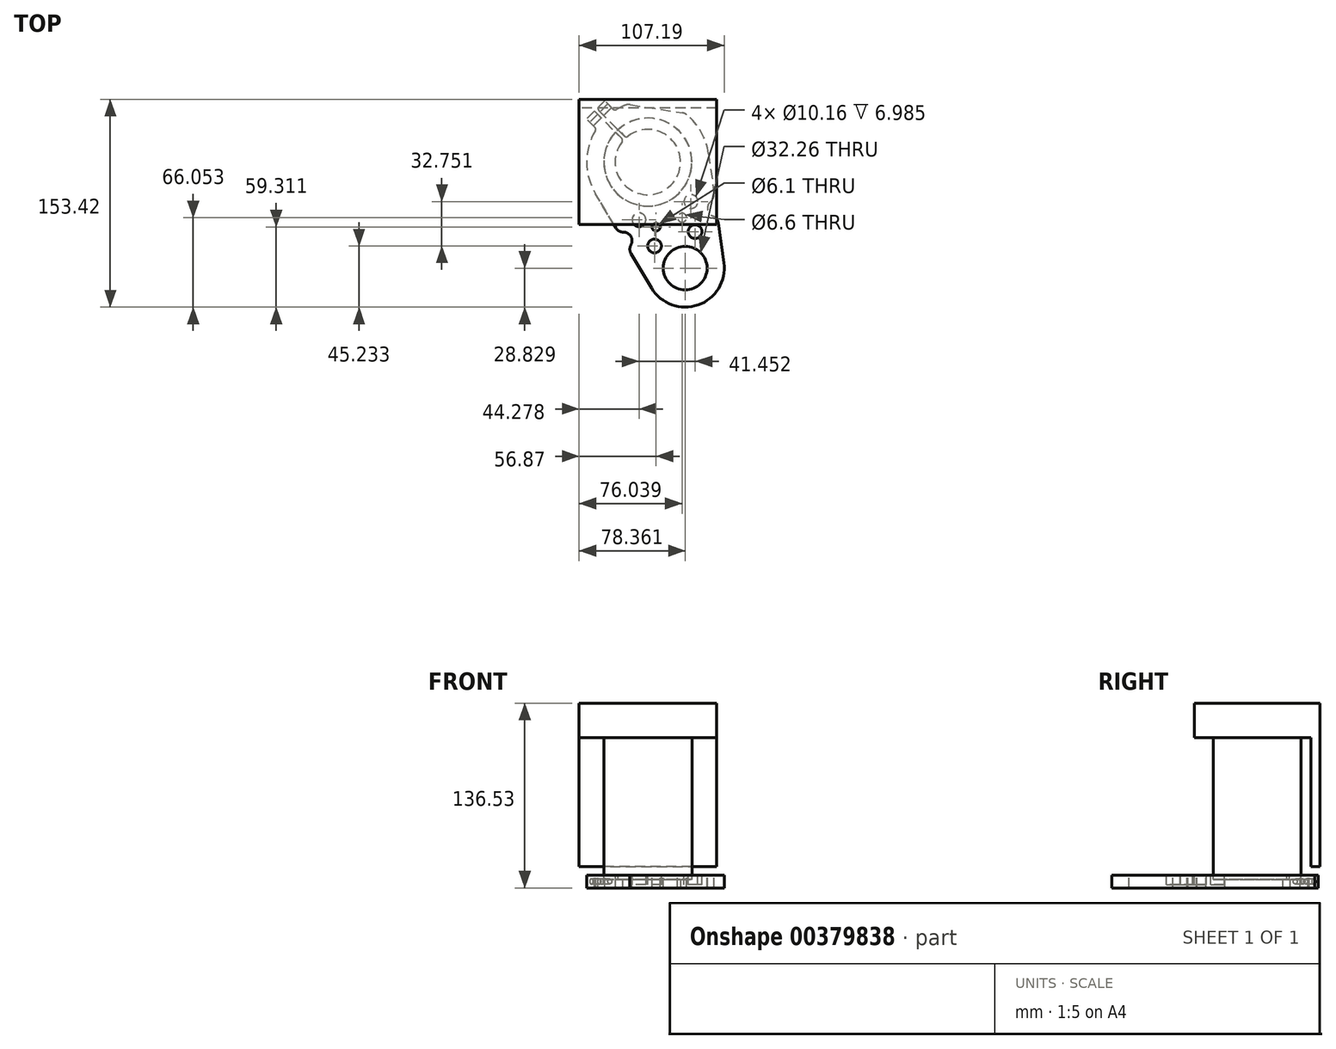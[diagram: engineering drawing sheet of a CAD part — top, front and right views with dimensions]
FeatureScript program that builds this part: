
annotation { "Feature Type Name" : "Feature", "Feature Type Description" : "" }
export const myFeature = defineFeature(function(context is Context, id is Id, definition is map)
    precondition{}
    {
        {
            var Q0;
            Q0=qCreatedBy(makeId("Top.planeOp"),FACE);
            var sketch = newSketch(context, id + "F0", { "sketchPlane" : qUnion([Q0])});
            skLineSegment(sketch, "E0.bottom", {"start": v(0, 0) * mm, "end": v(101.6, 0) * mm});
            skLineSegment(sketch, "E0.top", {"start": v(0, 152.4) * mm, "end": v(101.6, 152.4) * mm});
            skLineSegment(sketch, "E0.left", {"start": v(0, 0) * mm, "end": v(0, 152.4) * mm});
            skLineSegment(sketch, "E0.right", {"start": v(101.6, 0) * mm, "end": v(101.6, 152.4) * mm});
            skSolve(sketch);
        }
        {
            var Q0;
            Q0 = qSketchRegion(id + "F0", true);
            extrude(context, id + "F1", {"entities" : qUnion([Q0]), "depth" : 9.52 * mm});
        }
        {
            var Q0;
            Q0=makeQuery(id+"F1.opExtrude","CAP_FACE",FACE,{"disambiguationData":[OSD([sQuery(id+"F0.wireOp",EDGE,"E0.bottom"),sQuery(id+"F0.wireOp",EDGE,"E0.top"),sQuery(id+"F0.wireOp",EDGE,"E0.left"),sQuery(id+"F0.wireOp",EDGE,"E0.right")])],"isStart":false});
            var sketch = newSketch(context, id + "F2", { "sketchPlane" : qUnion([Q0])});
            skCircle(sketch, "E1", {"center": v(45.21, 107.19) * mm, "radius": 32.51 * mm});
            skCircle(sketch, "E2", {"center": v(72.77, 28.83) * mm, "radius": 16.13 * mm});
            skLineSegment(sketch, "E3", {"start": v(29.31, 152.4) * mm, "end": v(82.91, 0) * mm, "construction": true});
            skLineSegment(sketch, "E4", {"start": v(0, 152.4) * mm, "end": v(22.22, 130.18) * mm, "construction": true});
            skSolve(sketch);
        }
        {
            var Q0;
            Q0 = qSketchRegion(id + "F2", true);
            extrude(context, id + "F3", {"entities" : qUnion([Q0]), "operationType" : NewBodyOperationType.REMOVE, "oppositeDirection" : true, "depth" : 25.4 * mm});
        }
        {
            var Q0;
            Q0=makeQuery(id+"F1.opExtrude","CAP_FACE",FACE,{"disambiguationData":[OSD([sQuery(id+"F0.wireOp",EDGE,"E0.bottom"),sQuery(id+"F0.wireOp",EDGE,"E0.top"),sQuery(id+"F0.wireOp",EDGE,"E0.left"),sQuery(id+"F0.wireOp",EDGE,"E0.right")])],"isStart":false});
            var sketch = newSketch(context, id + "F4", { "sketchPlane" : qUnion([Q0])});
            skArc(sketch, "E5", {"start": v(89.98, 113.48) * mm, "mid": v(84.17, 130.12) * mm, "end": v(72.44, 143.28) * mm});
            skArc(sketch, "E6", {"start": v(48, 14.09) * mm, "mid": v(82.34, 1.63) * mm, "end": v(101.32, 32.84) * mm});
            skLineSegment(sketch, "E7", {"start": v(48, 14.09) * mm, "end": v(30.42, 43.62) * mm});
            skLineSegment(sketch, "E8", {"start": v(89.98, 113.48) * mm, "end": v(94.77, 79.45) * mm});
            skLineSegment(sketch, "E9", {"start": v(0, 152.4) * mm, "end": v(22.22, 130.18) * mm, "construction": true});
            skLineSegment(sketch, "E10", {"start": v(7.22, 131.7) * mm, "end": v(0, 138.93) * mm});
            skLineSegment(sketch, "E11", {"start": v(20.7, 145.18) * mm, "end": v(13.47, 152.4) * mm});
            skLineSegment(sketch, "E12", {"start": v(13.47, 152.4) * mm, "end": v(0, 138.93) * mm});
            skArc(sketch, "E13.trimOffspring", {"start": v(7.22, 131.7) * mm, "mid": v(0, 108.01) * mm, "end": v(6.36, 84.07) * mm});
            skArc(sketch, "E14", {"start": v(94.77, 79.45) * mm, "mid": v(89.36, 72.28) * mm, "end": v(96.54, 66.87) * mm});
            skArc(sketch, "E15", {"start": v(23.93, 54.54) * mm, "mid": v(32.63, 52.33) * mm, "end": v(30.42, 43.62) * mm});
            skLineSegment(sketch, "E16.trimOffspring", {"start": v(96.54, 66.87) * mm, "end": v(101.32, 32.84) * mm});
            skLineSegment(sketch, "E17.trimOffspring", {"start": v(23.93, 54.54) * mm, "end": v(6.36, 84.07) * mm});
            skLineSegment(sketch, "E18", {"start": v(30.35, 149.89) * mm, "end": v(72.44, 143.28) * mm});
            skArc(sketch, "E19.trimOffspring", {"start": v(30.35, 149.89) * mm, "mid": v(25.38, 147.82) * mm, "end": v(20.7, 145.18) * mm});
            skSolve(sketch);
        }
        {
            var Q0;
            {var subQ6=sQuery(id+"F4.wireOp",EDGE,"E7");Q0=makeQuery(id+"F4.imprint","IMPRINT",FACE,{"disambiguationData":[TD([[makeQuery(id+"F4.imprint","IMPRINT",EDGE,{"derivedFrom":subQ6}),1.0]])]});}
            var Q1;
            {var subQ0=sQuery(id+"F4.wireOp",EDGE,"E10");Q1=makeQuery(id+"F4.imprint","IMPRINT",FACE,{"disambiguationData":[TD([[makeQuery(id+"F4.imprint","IMPRINT",EDGE,{"derivedFrom":subQ0}),1.0]])]});}
            var Q2;
            {var subQ0=sQuery(id+"F4.wireOp",EDGE,"E12");Q2=makeQuery(id+"F4.imprint","IMPRINT",FACE,{"disambiguationData":[TD([[makeQuery(id+"F4.imprint","IMPRINT",EDGE,{"derivedFrom":subQ0}),-1.0]])]});}
            var Q3;
            {var subQ0=sQuery(id+"F4.wireOp",EDGE,"E11");Q3=makeQuery(id+"F4.imprint","IMPRINT",FACE,{"disambiguationData":[TD([[makeQuery(id+"F4.imprint","IMPRINT",EDGE,{"derivedFrom":subQ0}),-1.0]])]});}
            var Q4;
            {var subQ5=sQuery(id+"F4.wireOp",EDGE,"E8");Q4=makeQuery(id+"F4.imprint","IMPRINT",FACE,{"disambiguationData":[TD([[makeQuery(id+"F4.imprint","IMPRINT",EDGE,{"derivedFrom":subQ5}),1.0]])]});}
            var Q5;
            {var subQ0=sQuery(id+"F4.wireOp",EDGE,"E6");var subQ1=makeQuery(id+"F1.opExtrude","CAP_EDGE",EDGE,{"disambiguationData":[OSD([sQuery(id+"F0.wireOp",EDGE,"E0.bottom")])],"isStart":false});var subQ2=makeQuery(id+"F4.imprint","INTERSECT",VERTEX,{"derivedFrom":[subQ1,subQ0]});Q5=makeQuery(id+"F4.imprint","IMPRINT",FACE,{"disambiguationData":[TD([[makeQuery(id+"F4.imprint","IMPRINT",EDGE,{"disambiguationData":[TD([[subQ2,-1.0]])],"derivedFrom":subQ0}),-1.0]])]});}
            extrude(context, id + "F5", {"entities" : qUnion([Q0, Q1, Q2, Q3, Q4, Q5]), "operationType" : NewBodyOperationType.REMOVE, "oppositeDirection" : true, "depth" : 25.4 * mm});
        }
        {
            var Q0;
            Q0=makeQuery(id+"F1.opExtrude","CAP_FACE",FACE,{"disambiguationData":[OSD([sQuery(id+"F0.wireOp",EDGE,"E0.bottom"),sQuery(id+"F0.wireOp",EDGE,"E0.top"),sQuery(id+"F0.wireOp",EDGE,"E0.left"),sQuery(id+"F0.wireOp",EDGE,"E0.right")])],"isStart":true});
            var sketch = newSketch(context, id + "F6", { "sketchPlane" : qUnion([Q0])});
            skCircle(sketch, "E20", {"center": v(45.21, -107.19) * mm, "radius": 33.02 * mm});
            skCircle(sketch, "E21", {"center": v(45.21, -107.19) * mm, "radius": 24.13 * mm});
            skSolve(sketch);
        }
        {
            var Q0;
            Q0 = qSketchRegion(id + "F6", true);
            extrude(context, id + "F7", {"entities" : qUnion([Q0]), "operationType" : NewBodyOperationType.ADD, "oppositeDirection" : true, "depth" : 6.35 * mm});
        }
        {
            var Q0;
            Q0=makeQuery(id+"F1.opExtrude","CAP_FACE",FACE,{"disambiguationData":[OSD([sQuery(id+"F0.wireOp",EDGE,"E0.bottom"),sQuery(id+"F0.wireOp",EDGE,"E0.top"),sQuery(id+"F0.wireOp",EDGE,"E0.left"),sQuery(id+"F0.wireOp",EDGE,"E0.right")])],"isStart":false});
            var sketch = newSketch(context, id + "F8", { "sketchPlane" : qUnion([Q0])});
            skLineSegment(sketch, "E22", {"start": v(6.74, 145.66) * mm, "end": v(22.22, 130.18) * mm, "construction": true});
            skLineSegment(sketch, "E23", {"start": v(7.63, 146.56) * mm, "end": v(5.84, 144.77) * mm});
            skLineSegment(sketch, "E24", {"start": v(7.63, 146.56) * mm, "end": v(29.63, 124.56) * mm});
            skLineSegment(sketch, "E25", {"start": v(29.63, 124.56) * mm, "end": v(27.84, 122.77) * mm});
            skLineSegment(sketch, "E26", {"start": v(5.84, 144.77) * mm, "end": v(27.84, 122.77) * mm});
            skSolve(sketch);
        }
        {
            var Q0;
            Q0 = qSketchRegion(id + "F8", true);
            extrude(context, id + "F9", {"entities" : qUnion([Q0]), "operationType" : NewBodyOperationType.REMOVE, "oppositeDirection" : true, "depth" : 25.4 * mm});
        }
        {
            var Q0;
            Q0=makeQuery(id+"F5.boolean.opBoolean","COPY",FACE,{"derivedFrom":makeQuery(id+"F5.opExtrude","SWEPT_FACE",FACE,{"disambiguationData":[OSD([sQuery(id+"F4.wireOp",EDGE,"E10")])]})});
            var sketch = newSketch(context, id + "F10", { "sketchPlane" : qUnion([Q0])});
            skCircle(sketch, "E27", {"center": v(-93.13, 4.76) * mm, "radius": 1.9 * mm});
            skPoint(sketch, "E27.centerSnap0", {"position": v(-98.24, 4.76) * mm});
            skPoint(sketch, "E27.centerSnap1", {"position": v(-93.13, 9.53) * mm});
            skSolve(sketch);
        }
        {
            var Q0;
            Q0 = qSketchRegion(id + "F10", true);
            extrude(context, id + "F11", {"entities" : qUnion([Q0]), "operationType" : NewBodyOperationType.REMOVE, "oppositeDirection" : true, "depth" : 25.4 * mm});
        }
        {
            var Q0;
            Q0=makeQuery(id+"F1.opExtrude","CAP_FACE",FACE,{"disambiguationData":[OSD([sQuery(id+"F0.wireOp",EDGE,"E0.bottom"),sQuery(id+"F0.wireOp",EDGE,"E0.top"),sQuery(id+"F0.wireOp",EDGE,"E0.left"),sQuery(id+"F0.wireOp",EDGE,"E0.right")])],"isStart":false});
            var sketch = newSketch(context, id + "F12", { "sketchPlane" : qUnion([Q0])});
            skCircle(sketch, "E28", {"center": v(38.69, 64.5) * mm, "radius": 5.08 * mm});
            skCircle(sketch, "E29", {"center": v(77.02, 77.98) * mm, "radius": 5.08 * mm});
            skCircle(sketch, "E30", {"center": v(80.14, 55.78) * mm, "radius": 5.08 * mm});
            skCircle(sketch, "E31", {"center": v(50.15, 45.23) * mm, "radius": 5.08 * mm});
            skPoint(sketch, "E32", {"position": v(72.77, 28.83) * mm});
            skPoint(sketch, "E33", {"position": v(45.21, 107.19) * mm});
            skLineSegment(sketch, "E34", {"start": v(45.21, 107.19) * mm, "end": v(72.77, 28.83) * mm, "construction": true});
            skSolve(sketch);
        }
        {
            var Q0;
            Q0 = qSketchRegion(id + "F12", true);
            extrude(context, id + "F13", {"entities" : qUnion([Q0]), "operationType" : NewBodyOperationType.REMOVE, "oppositeDirection" : true, "depth" : 7 * mm});
        }
        {
            var Q0;
            Q0=makeQuery(id+"F1.opExtrude","CAP_FACE",FACE,{"disambiguationData":[OSD([sQuery(id+"F0.wireOp",EDGE,"E0.bottom"),sQuery(id+"F0.wireOp",EDGE,"E0.top"),sQuery(id+"F0.wireOp",EDGE,"E0.left"),sQuery(id+"F0.wireOp",EDGE,"E0.right")])],"isStart":false});
            var sketch = newSketch(context, id + "F14", { "sketchPlane" : qUnion([Q0])});
            skCircle(sketch, "E35", {"center": v(70.45, 66.05) * mm, "radius": 3.3 * mm});
            skCircle(sketch, "E36", {"center": v(51.28, 59.31) * mm, "radius": 3.05 * mm});
            skLineSegment(sketch, "E37", {"start": v(45.21, 107.19) * mm, "end": v(72.77, 28.83) * mm, "construction": true});
            skSolve(sketch);
        }
        {
            var Q0;
            Q0 = qSketchRegion(id + "F14", true);
            extrude(context, id + "F15", {"entities" : qUnion([Q0]), "operationType" : NewBodyOperationType.REMOVE, "oppositeDirection" : true, "depth" : 25.4 * mm});
        }
        {
            var Q0;
            Q0=makeQuery(id+"F1.opExtrude","CAP_FACE",FACE,{"disambiguationData":[OSD([sQuery(id+"F0.wireOp",EDGE,"E0.bottom"),sQuery(id+"F0.wireOp",EDGE,"E0.top"),sQuery(id+"F0.wireOp",EDGE,"E0.left"),sQuery(id+"F0.wireOp",EDGE,"E0.right")])],"isStart":false});
            var sketch = newSketch(context, id + "F16", { "sketchPlane" : qUnion([Q0])});
            skCircle(sketch, "E38", {"center": v(45.21, 107.19) * mm, "radius": 32.5 * mm});
            skSolve(sketch);
        }
        {
            var Q0;
            Q0 = qSketchRegion(id + "F16", true);
            extrude(context, id + "F17", {"entities" : qUnion([Q0]), "depth" : 101.6 * mm});
        }
        {
            var Q0;
            Q0=makeQuery(id+"F17.opExtrude","CAP_FACE",FACE,{"disambiguationData":[OSD([sQuery(id+"F16.wireOp",EDGE,"E38")])],"isStart":false});
            var sketch = newSketch(context, id + "F18", { "sketchPlane" : qUnion([Q0])});
            skLineSegment(sketch, "E39.bottom", {"start": v(-5.59, 153.42) * mm, "end": v(96.01, 153.42) * mm});
            skLineSegment(sketch, "E39.top", {"start": v(-5.59, 60.96) * mm, "end": v(96.01, 60.96) * mm});
            skLineSegment(sketch, "E39.left", {"start": v(-5.59, 153.42) * mm, "end": v(-5.59, 60.96) * mm});
            skLineSegment(sketch, "E39.right", {"start": v(96.01, 153.42) * mm, "end": v(96.01, 60.96) * mm});
            skPoint(sketch, "E39.middle", {"position": v(45.21, 107.19) * mm});
            skSolve(sketch);
        }
        {
            var Q0;
            Q0 = qSketchRegion(id + "F18", true);
            extrude(context, id + "F19", {"entities" : qUnion([Q0]), "operationType" : NewBodyOperationType.ADD, "depth" : 25.4 * mm});
        }
        {
            var Q0;
            Q0=makeQuery(id+"F19.opExtrude","CAP_FACE",FACE,{"disambiguationData":[OSD([sQuery(id+"F18.wireOp",EDGE,"E39.bottom"),sQuery(id+"F18.wireOp",EDGE,"E39.top"),sQuery(id+"F18.wireOp",EDGE,"E39.left"),sQuery(id+"F18.wireOp",EDGE,"E39.right")])],"isStart":true});
            var sketch = newSketch(context, id + "F20", { "sketchPlane" : qUnion([Q0])});
            skLineSegment(sketch, "E40.bottom", {"start": v(96.01, -153.42) * mm, "end": v(-5.59, -153.42) * mm});
            skLineSegment(sketch, "E40.top", {"start": v(96.01, -147.07) * mm, "end": v(-5.59, -147.07) * mm});
            skLineSegment(sketch, "E40.left", {"start": v(96.01, -153.42) * mm, "end": v(96.01, -147.07) * mm});
            skLineSegment(sketch, "E40.right", {"start": v(-5.59, -153.42) * mm, "end": v(-5.59, -147.07) * mm});
            skSolve(sketch);
        }
        {
            var Q0;
            Q0 = qSketchRegion(id + "F20", true);
            extrude(context, id + "F21", {"entities" : qUnion([Q0]), "operationType" : NewBodyOperationType.ADD, "depth" : 95.25 * mm});
        }
        {
            var Q0;
            Q0=makeQuery(id+"F5.boolean.opBoolean","COPY",EDGE,{"derivedFrom":makeQuery(id+"F5.opExtrude","SWEPT_EDGE",EDGE,{"disambiguationData":[OSD([sQuery(id+"F4.wireOp",EDGE,"E8"),sQuery(id+"F4.wireOp",EDGE,"E14")])]})});
            var Q1;
            Q1=makeQuery(id+"F5.boolean.opBoolean","COPY",EDGE,{"derivedFrom":makeQuery(id+"F5.opExtrude","SWEPT_EDGE",EDGE,{"disambiguationData":[OSD([sQuery(id+"F4.wireOp",EDGE,"E14"),sQuery(id+"F4.wireOp",EDGE,"E16.trimOffspring")])]})});
            var Q2;
            Q2=makeQuery(id+"F5.boolean.opBoolean","COPY",EDGE,{"derivedFrom":makeQuery(id+"F5.opExtrude","SWEPT_EDGE",EDGE,{"disambiguationData":[OSD([sQuery(id+"F4.wireOp",EDGE,"E15"),sQuery(id+"F4.wireOp",EDGE,"E17.trimOffspring")])]})});
            var Q3;
            Q3=makeQuery(id+"F5.boolean.opBoolean","COPY",EDGE,{"derivedFrom":makeQuery(id+"F5.opExtrude","SWEPT_EDGE",EDGE,{"disambiguationData":[OSD([sQuery(id+"F4.wireOp",EDGE,"E7"),sQuery(id+"F4.wireOp",EDGE,"E15")])]})});
            var Q4;
            Q4=makeQuery(id+"F5.boolean.opBoolean","COPY",EDGE,{"derivedFrom":makeQuery(id+"F5.opExtrude","SWEPT_EDGE",EDGE,{"disambiguationData":[OSD([sQuery(id+"F4.wireOp",EDGE,"E5"),sQuery(id+"F4.wireOp",EDGE,"E18")])]})});
            var Q5;
            Q5=makeQuery(id+"F5.boolean.opBoolean","COPY",EDGE,{"derivedFrom":makeQuery(id+"F5.opExtrude","SWEPT_EDGE",EDGE,{"disambiguationData":[OSD([sQuery(id+"F4.wireOp",EDGE,"E18"),sQuery(id+"F4.wireOp",EDGE,"E19.trimOffspring")])]})});
            fillet(context, id + "F22", {"entities" : qUnion([Q0, Q1, Q2, Q3, Q4, Q5]), "radius" : 6.35 * mm, "tangentPropagation" : true, "allowEdgeOverflow" : false});
        }
        {
            var Q0;
            {var subQ0=sQuery(id+"F4.wireOp",EDGE,"E12");var subQ1=sQuery(id+"F4.wireOp",EDGE,"E11");var subQ2=sQuery(id+"F0.wireOp",EDGE,"E0.top");Q0=makeQuery(id+"F5.boolean.opBoolean","TWEAK_EDGE",EDGE,{"derivedFrom":[makeQuery(id+"F5.opExtrude","SWEPT_EDGE",EDGE,{"disambiguationData":[OSD([subQ2,subQ1,subQ0]),ownerDisambiguation([makeQuery(id+"F4.imprint","IMPRINT",EDGE,{"derivedFrom":sQuery(id+"F4.wireOp",EDGE,"E5")})])]}),makeQuery(id+"F5.opExtrude","SWEPT_EDGE",EDGE,{"disambiguationData":[OSD([subQ2,subQ1,subQ0]),ownerDisambiguation([makeQuery(id+"F4.imprint","IMPRINT",EDGE,{"derivedFrom":subQ0})])]})]});}
            var Q1;
            Q1=makeQuery(id+"F9.boolean.opBoolean","COPY",EDGE,{"derivedFrom":makeQuery(id+"F9.opExtrude","SWEPT_EDGE",EDGE,{"disambiguationData":[OSD([sQuery(id+"F4.wireOp",EDGE,"E12"),sQuery(id+"F8.wireOp",EDGE,"E23"),sQuery(id+"F8.wireOp",EDGE,"E24")])]})});
            var Q2;
            Q2=makeQuery(id+"F9.boolean.opBoolean","COPY",EDGE,{"derivedFrom":makeQuery(id+"F9.opExtrude","SWEPT_EDGE",EDGE,{"disambiguationData":[OSD([sQuery(id+"F4.wireOp",EDGE,"E12"),sQuery(id+"F8.wireOp",EDGE,"E23"),sQuery(id+"F8.wireOp",EDGE,"E26")])]})});
            var Q3;
            {var subQ0=sQuery(id+"F4.wireOp",EDGE,"E12");var subQ1=sQuery(id+"F4.wireOp",EDGE,"E10");var subQ2=sQuery(id+"F0.wireOp",EDGE,"E0.left");Q3=makeQuery(id+"F5.boolean.opBoolean","TWEAK_EDGE",EDGE,{"derivedFrom":[makeQuery(id+"F5.opExtrude","SWEPT_EDGE",EDGE,{"disambiguationData":[OSD([subQ2,subQ1,subQ0]),ownerDisambiguation([makeQuery(id+"F4.imprint","IMPRINT",EDGE,{"derivedFrom":subQ1})])]}),makeQuery(id+"F5.opExtrude","SWEPT_EDGE",EDGE,{"disambiguationData":[OSD([subQ2,subQ1,subQ0]),ownerDisambiguation([makeQuery(id+"F4.imprint","IMPRINT",EDGE,{"derivedFrom":subQ0})])]})]});}
            var Q4;
            Q4=makeQuery(id+"F5.boolean.opBoolean","COPY",EDGE,{"derivedFrom":makeQuery(id+"F5.opExtrude","SWEPT_EDGE",EDGE,{"disambiguationData":[OSD([sQuery(id+"F4.wireOp",EDGE,"E10"),sQuery(id+"F4.wireOp",EDGE,"E13.trimOffspring")])]})});
            var Q5;
            Q5=makeQuery(id+"F5.boolean.opBoolean","COPY",EDGE,{"derivedFrom":makeQuery(id+"F5.opExtrude","SWEPT_EDGE",EDGE,{"disambiguationData":[OSD([sQuery(id+"F4.wireOp",EDGE,"E11"),sQuery(id+"F4.wireOp",EDGE,"E19.trimOffspring")])]})});
            var Q6;
            Q6=makeQuery(id+"F9.boolean.opBoolean","INTERSECT",EDGE,{"derivedFrom":[makeQuery(id+"F7.opExtrude","SWEPT_FACE",FACE,{"disambiguationData":[OSD([sQuery(id+"F6.wireOp",EDGE,"E21")])]}),makeQuery(id+"F9.opExtrude","SWEPT_FACE",FACE,{"disambiguationData":[OSD([sQuery(id+"F8.wireOp",EDGE,"E26")])]})]});
            var Q7;
            Q7=makeQuery(id+"F9.boolean.opBoolean","INTERSECT",EDGE,{"derivedFrom":[makeQuery(id+"F7.opExtrude","SWEPT_FACE",FACE,{"disambiguationData":[OSD([sQuery(id+"F6.wireOp",EDGE,"E21")])]}),makeQuery(id+"F9.opExtrude","SWEPT_FACE",FACE,{"disambiguationData":[OSD([sQuery(id+"F8.wireOp",EDGE,"E24")])]})]});
            fillet(context, id + "F23", {"entities" : qUnion([Q0, Q1, Q2, Q3, Q4, Q5, Q6, Q7]), "radius" : 2.03 * mm, "tangentPropagation" : true, "allowEdgeOverflow" : false});
        }
    });
